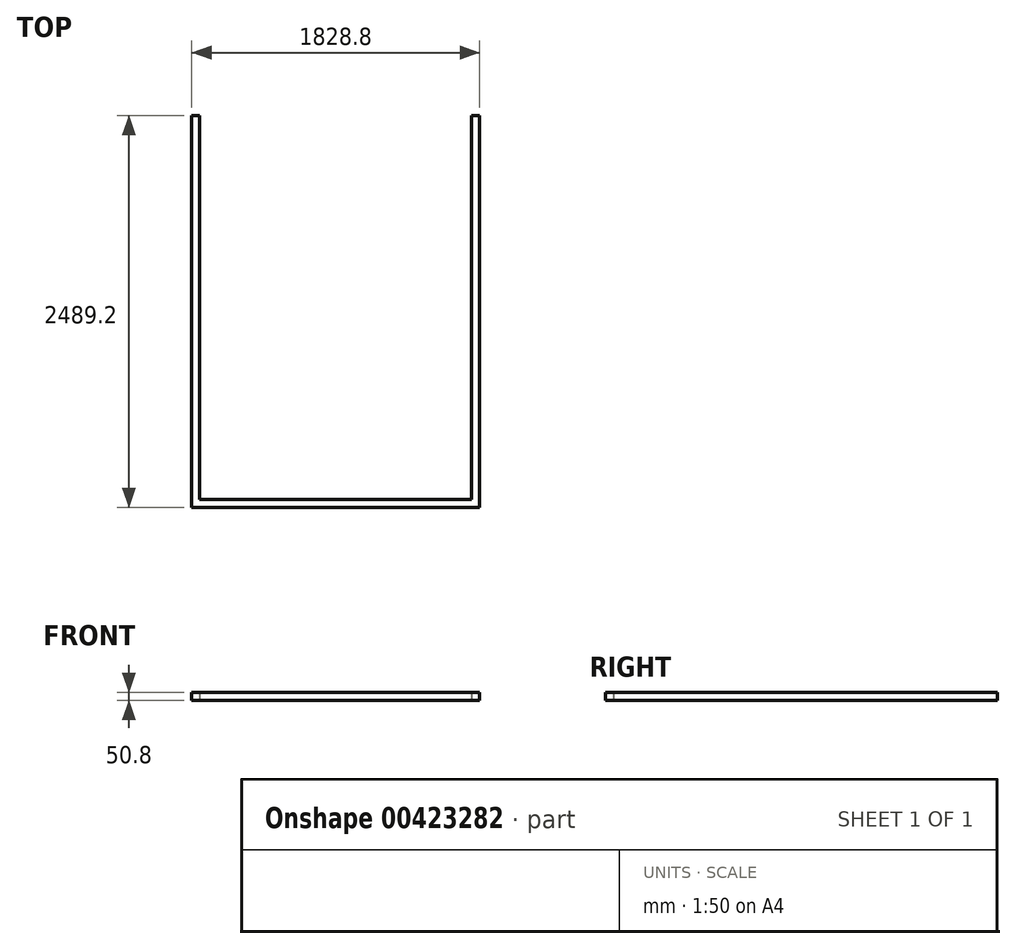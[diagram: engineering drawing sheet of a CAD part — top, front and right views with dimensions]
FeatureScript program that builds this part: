
annotation { "Feature Type Name" : "Feature", "Feature Type Description" : "" }
export const myFeature = defineFeature(function(context is Context, id is Id, definition is map)
    precondition{}
    {
        {
            var Q0;
            Q0=qCreatedBy(makeId("Front.planeOp"),FACE);
            var sketch = newSketch(context, id + "F0", { "sketchPlane" : qUnion([Q0])});
            skLineSegment(sketch, "E0.bottom", {"start": v(914.4, 25.4) * mm, "end": v(-914.4, 25.4) * mm});
            skLineSegment(sketch, "E0.top", {"start": v(914.4, -25.4) * mm, "end": v(-914.4, -25.4) * mm});
            skLineSegment(sketch, "E0.left", {"start": v(914.4, 25.4) * mm, "end": v(914.4, -25.4) * mm});
            skLineSegment(sketch, "E0.right", {"start": v(-914.4, 25.4) * mm, "end": v(-914.4, -25.4) * mm});
            skPoint(sketch, "E0.middle", {"position": v(0, 0) * mm});
            skSolve(sketch);
        }
        {
            var Q0;
            Q0=makeQuery(id+"F0.imprint","IMPRINT",FACE,{"disambiguationData":[TD([[makeQuery(id+"F0.imprint","IMPRINT",EDGE,{"derivedFrom":sQuery(id+"F0.wireOp",EDGE,"E0.bottom")}),1.0]])]});
            extrude(context, id + "F1", {"entities" : qUnion([Q0]), "depth" : 50.8 * mm});
        }
        {
            var Q0;
            Q0=makeQuery(id+"F1.opExtrude","CAP_FACE",FACE,{"disambiguationData":[OSD([sQuery(id+"F0.wireOp",EDGE,"E0.bottom"),sQuery(id+"F0.wireOp",EDGE,"E0.top"),sQuery(id+"F0.wireOp",EDGE,"E0.left"),sQuery(id+"F0.wireOp",EDGE,"E0.right")])],"isStart":true});
            var sketch = newSketch(context, id + "F2", { "sketchPlane" : qUnion([Q0])});
            skLineSegment(sketch, "E1.bottom", {"start": v(-914.4, 25.4) * mm, "end": v(-863.6, 25.4) * mm});
            skLineSegment(sketch, "E1.top", {"start": v(-914.4, -25.4) * mm, "end": v(-863.6, -25.4) * mm});
            skLineSegment(sketch, "E1.left", {"start": v(-914.4, 25.4) * mm, "end": v(-914.4, -25.4) * mm});
            skLineSegment(sketch, "E1.right", {"start": v(-863.6, 25.4) * mm, "end": v(-863.6, -25.4) * mm});
            skSolve(sketch);
        }
        {
            var Q0;
            Q0=makeQuery(id+"F2.imprint","IMPRINT",FACE,{"disambiguationData":[TD([[makeQuery(id+"F2.imprint","IMPRINT",EDGE,{"derivedFrom":sQuery(id+"F2.wireOp",EDGE,"E1.bottom")}),-1.0]])]});
            extrude(context, id + "F3", {"entities" : qUnion([Q0]), "operationType" : NewBodyOperationType.ADD, "depth" : 2438.4 * mm});
        }
        {
            var Q0;
            Q0=makeQuery(id+"F1.opExtrude","CAP_FACE",FACE,{"disambiguationData":[OSD([sQuery(id+"F0.wireOp",EDGE,"E0.bottom"),sQuery(id+"F0.wireOp",EDGE,"E0.top"),sQuery(id+"F0.wireOp",EDGE,"E0.left"),sQuery(id+"F0.wireOp",EDGE,"E0.right")])],"isStart":true});
            var sketch = newSketch(context, id + "F4", { "sketchPlane" : qUnion([Q0])});
            skLineSegment(sketch, "E2.bottom", {"start": v(914.4, 25.4) * mm, "end": v(863.6, 25.4) * mm});
            skLineSegment(sketch, "E2.top", {"start": v(914.4, -25.4) * mm, "end": v(863.6, -25.4) * mm});
            skLineSegment(sketch, "E2.left", {"start": v(914.4, 25.4) * mm, "end": v(914.4, -25.4) * mm});
            skLineSegment(sketch, "E2.right", {"start": v(863.6, 25.4) * mm, "end": v(863.6, -25.4) * mm});
            skSolve(sketch);
        }
        {
            var Q0;
            Q0=makeQuery(id+"F4.imprint","IMPRINT",FACE,{"disambiguationData":[TD([[makeQuery(id+"F4.imprint","IMPRINT",EDGE,{"derivedFrom":sQuery(id+"F4.wireOp",EDGE,"E2.bottom")}),-1.0]])]});
            extrude(context, id + "F5", {"entities" : qUnion([Q0]), "operationType" : NewBodyOperationType.ADD, "depth" : 2438.4 * mm});
        }
    });
